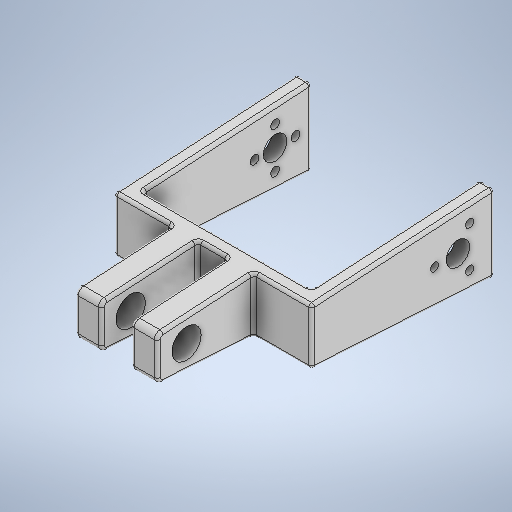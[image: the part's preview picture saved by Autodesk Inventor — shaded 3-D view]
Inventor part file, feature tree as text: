
AUTODESK INVENTOR PART (.ipt)
format: ipt  version: 2025.3 (Build 293356000, 356)  size: 440,320 bytes
history: native  units: in
note: dims shown in document units (in); Inventor stores cm internally (conversion verified against a paired STEP export)
features: sketch x8, hole x4, fillet x4, extrude x2
ambient origin geometry x8: Origin, YZ Plane, XZ Plane, XY Plane, X Axis, Y Axis, Z Axis, Center Point
bodies: Solid1 (feature_tree)
feature tree (18):
  extrude  "Extrusion1"  Depth=0.5906in
  hole  "Hole1"  [1 undecoded]
  extrude  "Extrusion2"  Depth=1.4961in
  hole  "Hole2"  [1 undecoded]
  fillet  "Fillet1"  [1 undecoded]
  fillet  "Fillet2"  Radius=0.7776in
  fillet  "Fillet3"  Radius=1.2992in
  hole  "Hole3"  [1 undecoded]
  hole  "Hole4"  [1 undecoded]
  fillet  "Fillet4"  Radius=0.0394in
  sketch  "Sketch1"  dims[d0=0.9843in d1=0.5906in]
  sketch  "Sketch3"  dims[d14=0.1969in d15=0.1969in d16=0.0in d17=0.0in d18=0.7776in d19=1.2992in]
  sketch  "Sketch4"  dims[d20=0.4016in d21=0.3937in]
  sketch  "Sketch5"  dims[d22=0.3937in d23=0.2362in d24=0.1575in d25=0.0787in d26=90.0deg d27=0.315in d28=0.8108in d29=0.0787in d30=0.0394in]
  sketch  "Sketch6"  dims[d31=0.0394in]
  sketch  "Sketch Circular Pattern1"  dims[d2=3.2677in d3=2.6575in d4=0.0in]
  sketch  "Sketch7"  dims[d32=0.2756in d33=1.5748in d35=360.0deg d37=0.1181in d38=0.2362in d39=0.1575in d40=0.0787in d41=90.0deg d42=0.315in d43=0.8108in d44=0.315in d45=1.1811in d47=360.0deg d49=0.1102in d50=0.2362in d51=0.1575in d52=0.0787in d53=90.0deg d54=0.315in d55=0.8108in d56=0.0394in]
  sketch  "Sketch Circular Pattern2"  dims[d5=0.315in d6=0.2362in d7=0.1575in d8=0.0787in d9=90.0deg d10=0.315in d11=0.8108in d13=1.4961in]
note: 5 required parameter values undecoded (feature->parameter linkage not recoverable at this tier; creation-order binding heuristic only, values carry confidence <= 0.55)
